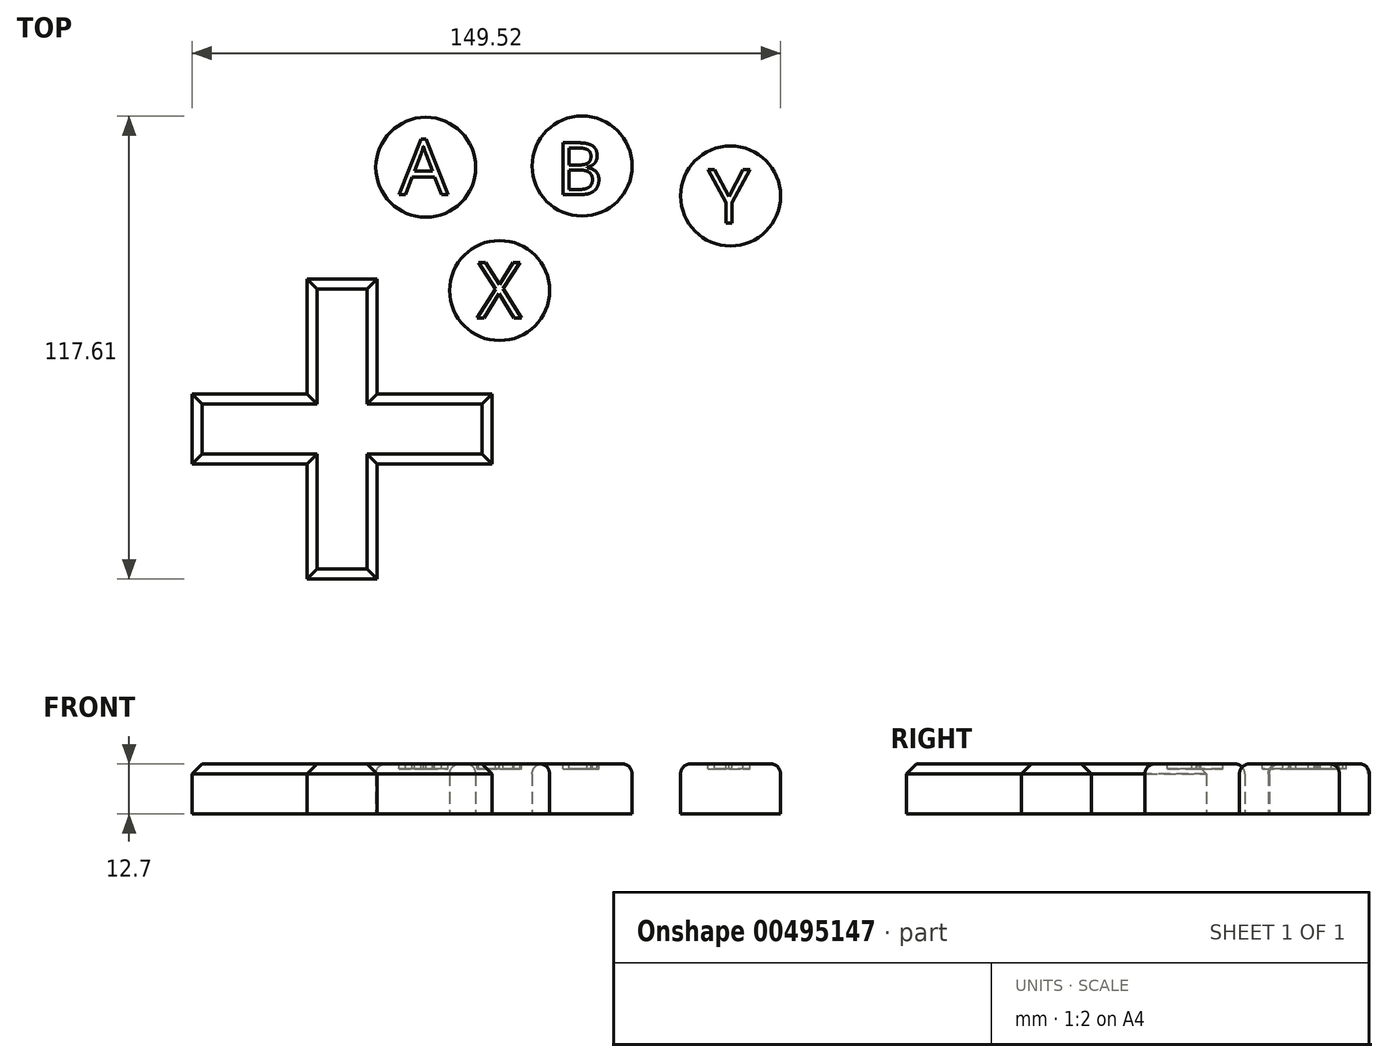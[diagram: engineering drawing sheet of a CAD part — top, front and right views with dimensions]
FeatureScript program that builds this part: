
annotation { "Feature Type Name" : "Feature", "Feature Type Description" : "" }
export const myFeature = defineFeature(function(context is Context, id is Id, definition is map)
    precondition{}
    {
        {
            var Q0;
            Q0=qCreatedBy(makeId("Top.planeOp"),FACE);
            var sketch = newSketch(context, id + "F0", { "sketchPlane" : qUnion([Q0])});
            skLineSegment(sketch, "E0", {"start": v(-37.24, 0) * mm, "end": v(-37.24, 8.89) * mm});
            skLineSegment(sketch, "E1", {"start": v(-37.24, 8.89) * mm, "end": v(-8.03, 8.89) * mm});
            skLineSegment(sketch, "E2", {"start": v(-8.03, 8.89) * mm, "end": v(-8.03, 38.1) * mm});
            skLineSegment(sketch, "E3", {"start": v(-8.03, 38.1) * mm, "end": v(9.75, 38.1) * mm});
            skLineSegment(sketch, "E4", {"start": v(9.75, 38.1) * mm, "end": v(9.75, 8.89) * mm});
            skLineSegment(sketch, "E5", {"start": v(9.75, 8.89) * mm, "end": v(38.96, 8.89) * mm});
            skLineSegment(sketch, "E6", {"start": v(38.96, 8.89) * mm, "end": v(38.96, 0) * mm});
            skLineSegment(sketch, "E7.MirrorCS", {"start": v(-37.24, 0) * mm, "end": v(-37.24, -8.89) * mm});
            skLineSegment(sketch, "E8.MirrorCS", {"start": v(-37.24, -8.89) * mm, "end": v(-8.03, -8.89) * mm});
            skLineSegment(sketch, "E9.MirrorCS", {"start": v(-8.03, -8.89) * mm, "end": v(-8.03, -38.1) * mm});
            skLineSegment(sketch, "E10.MirrorCS", {"start": v(-8.03, -38.1) * mm, "end": v(9.75, -38.1) * mm});
            skLineSegment(sketch, "E11.MirrorCS", {"start": v(9.75, -38.1) * mm, "end": v(9.75, -8.89) * mm});
            skLineSegment(sketch, "E12.MirrorCS", {"start": v(9.75, -8.89) * mm, "end": v(38.96, -8.89) * mm});
            skLineSegment(sketch, "E13.MirrorCS", {"start": v(38.96, -8.89) * mm, "end": v(38.96, 0) * mm});
            skSolve(sketch);
        }
        {
            var Q0;
            Q0=makeQuery(id+"F0.imprint","IMPRINT",FACE,{"disambiguationData":[TD([[makeQuery(id+"F0.imprint","IMPRINT",EDGE,{"derivedFrom":sQuery(id+"F0.wireOp",EDGE,"E0")}),-1.0]])]});
            extrude(context, id + "F1", {"entities" : qUnion([Q0]), "depth" : 12.7 * mm});
        }
        {
            var Q0;
            Q0=makeQuery(id+"F1.opExtrude","CAP_FACE",FACE,{"disambiguationData":[OSD([sQuery(id+"F0.wireOp",EDGE,"E0"),sQuery(id+"F0.wireOp",EDGE,"E1"),sQuery(id+"F0.wireOp",EDGE,"E2"),sQuery(id+"F0.wireOp",EDGE,"E3"),sQuery(id+"F0.wireOp",EDGE,"E4"),sQuery(id+"F0.wireOp",EDGE,"E5"),sQuery(id+"F0.wireOp",EDGE,"E6"),sQuery(id+"F0.wireOp",EDGE,"E7.MirrorCS"),sQuery(id+"F0.wireOp",EDGE,"E8.MirrorCS"),sQuery(id+"F0.wireOp",EDGE,"E9.MirrorCS"),sQuery(id+"F0.wireOp",EDGE,"E10.MirrorCS"),sQuery(id+"F0.wireOp",EDGE,"E11.MirrorCS"),sQuery(id+"F0.wireOp",EDGE,"E12.MirrorCS"),sQuery(id+"F0.wireOp",EDGE,"E13.MirrorCS")])],"isStart":false});
            chamfer(context, id + "F2", {"entities" : qUnion([Q0]), "width" : 2.54 * mm, "tangentPropagation" : true});
        }
        {
            var Q0;
            Q0=qCreatedBy(makeId("Top.planeOp"),FACE);
            var sketch = newSketch(context, id + "F3", { "sketchPlane" : qUnion([Q0])});
            skCircle(sketch, "E14", {"center": v(40.92, 35.16) * mm, "radius": 12.7 * mm});
            skCircle(sketch, "E15", {"center": v(22.16, 66.48) * mm, "radius": 12.7 * mm});
            skCircle(sketch, "E16", {"center": v(61.86, 66.8) * mm, "radius": 12.7 * mm});
            skCircle(sketch, "E17", {"center": v(99.58, 59.2) * mm, "radius": 12.7 * mm});
            skSolve(sketch);
        }
        {
            var Q0;
            Q0=makeQuery(id+"F3.imprint","IMPRINT",FACE,{"disambiguationData":[TD([[makeQuery(id+"F3.imprint","IMPRINT",EDGE,{"derivedFrom":sQuery(id+"F3.wireOp",EDGE,"E15")}),1.0]])]});
            var Q1;
            Q1=makeQuery(id+"F3.imprint","IMPRINT",FACE,{"disambiguationData":[TD([[makeQuery(id+"F3.imprint","IMPRINT",EDGE,{"derivedFrom":sQuery(id+"F3.wireOp",EDGE,"E16")}),1.0]])]});
            var Q2;
            Q2=makeQuery(id+"F3.imprint","IMPRINT",FACE,{"disambiguationData":[TD([[makeQuery(id+"F3.imprint","IMPRINT",EDGE,{"derivedFrom":sQuery(id+"F3.wireOp",EDGE,"E17")}),1.0]])]});
            var Q3;
            Q3=makeQuery(id+"F3.imprint","IMPRINT",FACE,{"disambiguationData":[TD([[makeQuery(id+"F3.imprint","IMPRINT",EDGE,{"derivedFrom":sQuery(id+"F3.wireOp",EDGE,"E14")}),1.0]])]});
            extrude(context, id + "F4", {"entities" : qUnion([Q0, Q1, Q2, Q3]), "depth" : 12.7 * mm});
        }
        {
            var Q0;
            Q0=makeQuery(id+"F4.opExtrude","CAP_FACE",FACE,{"disambiguationData":[OSD([sQuery(id+"F3.wireOp",EDGE,"E15")])],"isStart":false});
            var sketch = newSketch(context, id + "F5", { "sketchPlane" : qUnion([Q0])});
            skText(sketch, "E18", { "text": "A\n", "fontName": "OpenSans-Regular.ttf"});
            const initialGuessF5  = {"E18": [0.01534, 0.05957, 1, 0, 0.01416]};
            skSetInitialGuess(sketch, initialGuessF5);
            skSolve(sketch);
        }
        {
            var Q0;
            Q0=makeQuery(id+"F5.imprint","IMPRINT",FACE,{"disambiguationData":[TD([[makeQuery(id+"F5.imprint","IMPRINT",EDGE,{"derivedFrom":sQuery(id+"F5.wireOp",EDGE,"E18.sketch_text.stroke-0")}),-1.0]])]});
            extrude(context, id + "F6", {"entities" : qUnion([Q0]), "operationType" : NewBodyOperationType.REMOVE, "oppositeDirection" : true, "depth" : 1.27 * mm});
        }
        {
            var Q0;
            Q0=makeQuery(id+"F4.opExtrude","CAP_EDGE",EDGE,{"disambiguationData":[OSD([sQuery(id+"F3.wireOp",EDGE,"E15")])],"isStart":false});
            fillet(context, id + "F7", {"entities" : qUnion([Q0]), "radius" : 2.54 * mm, "tangentPropagation" : true, "allowEdgeOverflow" : false});
        }
        {
            var Q0;
            Q0=makeQuery(id+"F4.opExtrude","CAP_FACE",FACE,{"disambiguationData":[OSD([sQuery(id+"F3.wireOp",EDGE,"E16")])],"isStart":false});
            var sketch = newSketch(context, id + "F8", { "sketchPlane" : qUnion([Q0])});
            skText(sketch, "E19", { "text": "B", "fontName": "OpenSans-Regular.ttf"});
            const initialGuessF8  = {"E19": [0.0552, 0.05955, 1, 0, 0.01328]};
            skSetInitialGuess(sketch, initialGuessF8);
            skSolve(sketch);
        }
        {
            var Q0;
            Q0=makeQuery(id+"F8.imprint","IMPRINT",FACE,{"disambiguationData":[TD([[makeQuery(id+"F8.imprint","IMPRINT",EDGE,{"derivedFrom":sQuery(id+"F8.wireOp",EDGE,"E19.sketch_text.stroke-0")}),-1.0]])]});
            extrude(context, id + "F9", {"entities" : qUnion([Q0]), "operationType" : NewBodyOperationType.REMOVE, "oppositeDirection" : true, "depth" : 1.27 * mm});
        }
        {
            var Q0;
            Q0=makeQuery(id+"F4.opExtrude","CAP_EDGE",EDGE,{"disambiguationData":[OSD([sQuery(id+"F3.wireOp",EDGE,"E16")])],"isStart":false});
            fillet(context, id + "F10", {"entities" : qUnion([Q0]), "radius" : 2.54 * mm, "tangentPropagation" : true, "allowEdgeOverflow" : false});
        }
        {
            var Q0;
            Q0=makeQuery(id+"F4.opExtrude","CAP_FACE",FACE,{"disambiguationData":[OSD([sQuery(id+"F3.wireOp",EDGE,"E17")])],"isStart":false});
            var sketch = newSketch(context, id + "F11", { "sketchPlane" : qUnion([Q0])});
            skText(sketch, "E20", { "text": "Y\n", "fontName": "OpenSans-Regular.ttf"});
            const initialGuessF11  = {"E20": [0.09383, 0.05228, 1, 0, 0.01372]};
            skSetInitialGuess(sketch, initialGuessF11);
            skSolve(sketch);
        }
        {
            var Q0;
            Q0=makeQuery(id+"F11.imprint","IMPRINT",FACE,{"disambiguationData":[TD([[makeQuery(id+"F11.imprint","IMPRINT",EDGE,{"derivedFrom":sQuery(id+"F11.wireOp",EDGE,"E20.sketch_text.stroke-0")}),-1.0]])]});
            extrude(context, id + "F12", {"entities" : qUnion([Q0]), "operationType" : NewBodyOperationType.REMOVE, "oppositeDirection" : true, "depth" : 1.27 * mm});
        }
        {
            var Q0;
            Q0=makeQuery(id+"F4.opExtrude","CAP_FACE",FACE,{"disambiguationData":[OSD([sQuery(id+"F3.wireOp",EDGE,"E14")])],"isStart":false});
            var sketch = newSketch(context, id + "F13", { "sketchPlane" : qUnion([Q0])});
            skText(sketch, "E21", { "text": "X", "fontName": "OpenSans-Regular.ttf"});
            const initialGuessF13  = {"E21": [0.03512, 0.0282, 1, 0, 0.01422]};
            skSetInitialGuess(sketch, initialGuessF13);
            skSolve(sketch);
        }
        {
            var Q0;
            Q0=makeQuery(id+"F13.imprint","IMPRINT",FACE,{"disambiguationData":[TD([[makeQuery(id+"F13.imprint","IMPRINT",EDGE,{"derivedFrom":sQuery(id+"F13.wireOp",EDGE,"E21.sketch_text.stroke-0")}),-1.0]])]});
            extrude(context, id + "F14", {"entities" : qUnion([Q0]), "operationType" : NewBodyOperationType.REMOVE, "oppositeDirection" : true, "depth" : 1.27 * mm});
        }
        {
            var Q0;
            Q0=makeQuery(id+"F4.opExtrude","CAP_EDGE",EDGE,{"disambiguationData":[OSD([sQuery(id+"F3.wireOp",EDGE,"E14")])],"isStart":false});
            var Q1;
            Q1=makeQuery(id+"F4.opExtrude","CAP_EDGE",EDGE,{"disambiguationData":[OSD([sQuery(id+"F3.wireOp",EDGE,"E17")])],"isStart":false});
            fillet(context, id + "F15", {"entities" : qUnion([Q0, Q1]), "radius" : 2.54 * mm, "tangentPropagation" : true, "allowEdgeOverflow" : false});
        }
    });
